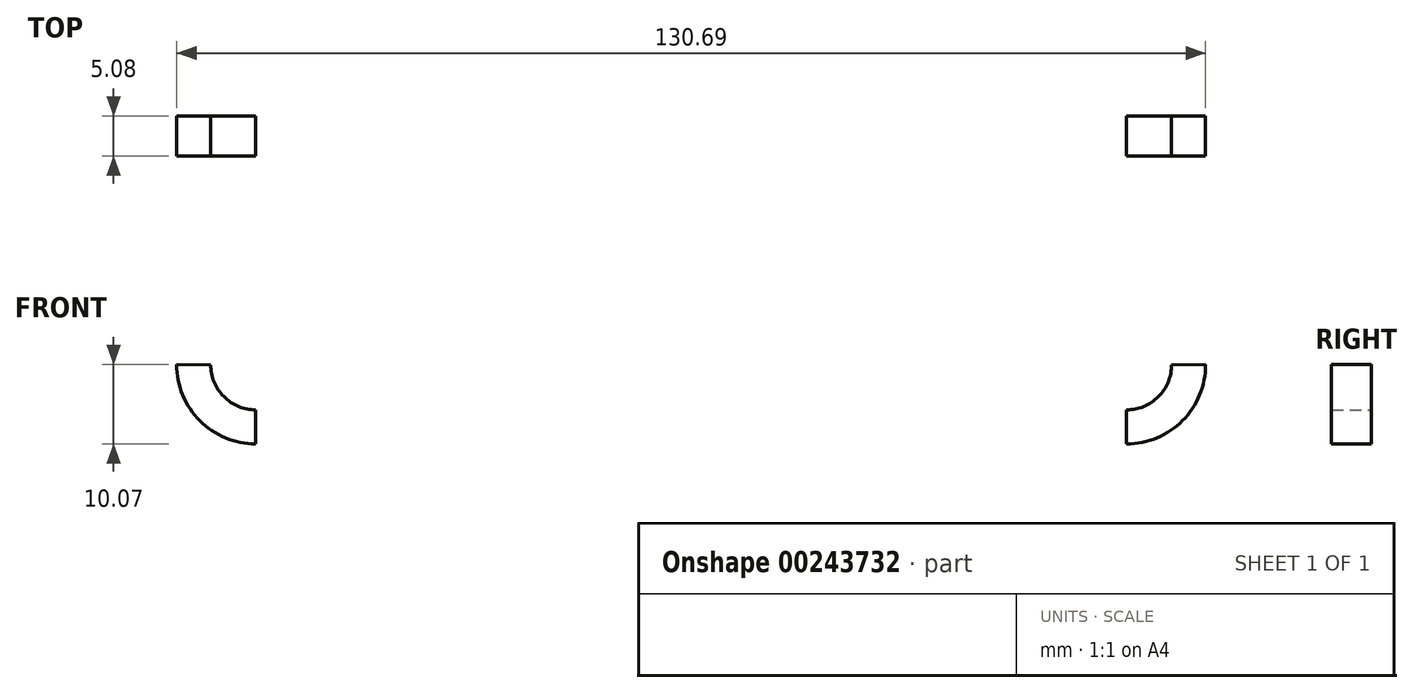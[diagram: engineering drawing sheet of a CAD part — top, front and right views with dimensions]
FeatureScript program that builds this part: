
annotation { "Feature Type Name" : "Feature", "Feature Type Description" : "" }
export const myFeature = defineFeature(function(context is Context, id is Id, definition is map)
    precondition{}
    {
        {
            var Q0;
            Q0=qCreatedBy(makeId("Front.planeOp"),FACE);
            var sketch = newSketch(context, id + "F0", { "sketchPlane" : qUnion([Q0])});
            skLineSegment(sketch, "E0", {"start": v(-29.35, 17.54) * mm, "end": v(25.95, 17.54) * mm});
            skArc(sketch, "E1", {"start": v(25.95, 17.54) * mm, "mid": v(30, 19.22) * mm, "end": v(31.67, 23.27) * mm});
            skArc(sketch, "E2.0", {"start": v(25.95, 13.22) * mm, "mid": v(33.06, 16.17) * mm, "end": v(35.99, 23.3) * mm});
            skLineSegment(sketch, "E3", {"start": v(31.67, 23.27) * mm, "end": v(35.99, 23.3) * mm});
            skLineSegment(sketch, "E4", {"start": v(25.95, 13.22) * mm, "end": v(-29.35, 13.22) * mm});
            skLineSegment(sketch, "E5", {"start": v(-29.35, 17.54) * mm, "end": v(-29.35, 13.22) * mm});
            skLineSegment(sketch, "E6.MirrorCS", {"start": v(-90.38, 23.27) * mm, "end": v(-94.7, 23.3) * mm});
            skLineSegment(sketch, "E7.MirrorCS", {"start": v(-84.66, 13.22) * mm, "end": v(-29.35, 13.22) * mm});
            skLineSegment(sketch, "E8.MirrorCS", {"start": v(-29.35, 17.54) * mm, "end": v(-84.66, 17.54) * mm});
            skArc(sketch, "E9.MirrorCS", {"start": v(-84.66, 17.54) * mm, "mid": v(-88.71, 19.22) * mm, "end": v(-90.38, 23.27) * mm});
            skArc(sketch, "E10.MirrorCS", {"start": v(-84.66, 13.22) * mm, "mid": v(-91.77, 16.17) * mm, "end": v(-94.7, 23.3) * mm});
            skLineSegment(sketch, "E11", {"start": v(-84.66, 17.54) * mm, "end": v(-84.66, 13.22) * mm});
            skLineSegment(sketch, "E12", {"start": v(25.95, 17.54) * mm, "end": v(25.95, 13.22) * mm});
            skSolve(sketch);
        }
        {
            var Q0;
            Q0=makeQuery(id+"F0.imprint","IMPRINT",FACE,{"disambiguationData":[TD([[makeQuery(id+"F0.imprint","IMPRINT",EDGE,{"derivedFrom":sQuery(id+"F0.wireOp",EDGE,"E1")}),-1.0]])]});
            extrude(context, id + "F1", {"entities" : qUnion([Q0]), "depth" : 5.08 * mm});
        }
        {
            var Q0;
            Q0=makeQuery(id+"F0.imprint","IMPRINT",FACE,{"disambiguationData":[TD([[makeQuery(id+"F0.imprint","IMPRINT",EDGE,{"derivedFrom":sQuery(id+"F0.wireOp",EDGE,"E6.MirrorCS")}),1.0]])]});
            extrude(context, id + "F2", {"entities" : qUnion([Q0]), "depth" : 5.08 * mm});
        }
    });
